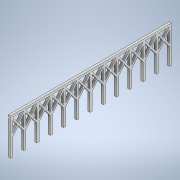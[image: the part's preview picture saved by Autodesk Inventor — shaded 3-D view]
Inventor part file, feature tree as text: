
AUTODESK INVENTOR PART (.ipt)
format: ipt  version: 2021 (Build 250183000, 183)  size: 289,280 bytes
history: native  units: in
note: dims shown in document units (in); Inventor stores cm internally (conversion verified against a paired STEP export)
features: sketch x2, extrude x1
ambient origin geometry x8: Origin, YZ Plane, XZ Plane, XY Plane, X Axis, Y Axis, Z Axis, Center Point
bodies: Solid1 (feature_tree)
feature tree (3):
  extrude  "Extrusion1"  Depth=10.0in
  sketch  "Sketch2"  dims[d2=156.0in d3=10.0in d4=4.7244in d6=60.0in d7=0.3937in d9=1.0in d11=4.7244in d13=60.0in d14=0.3937in d16=1.0in d18=10.0in d19=10.0in d20=0.0in]
  sketch  "Sketch1"  dims[d0=720.0in d1=10.0in]
